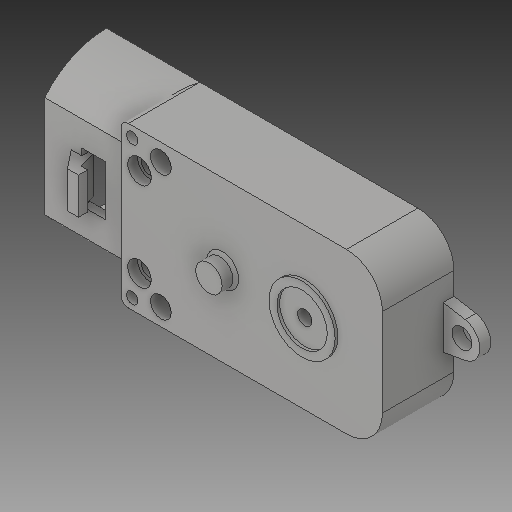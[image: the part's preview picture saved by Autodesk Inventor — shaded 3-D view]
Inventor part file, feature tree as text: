
AUTODESK INVENTOR PART (.ipt)
format: ipt  version: 2019 (Build 230136000, 136)  size: 182,784 bytes
history: mixed  units: mm
features: chamfer x1, imported_body x1
ambient origin geometry x8: Origin, YZ Plane, XZ Plane, XY Plane, X Axis, Y Axis, Z Axis, Center Point
bodies: Solid1 (imported_parasolid)
feature tree (2):
  chamfer  "Chamfer1"  [1 undecoded]
  imported_body  NMx_Import_Brep_tag  [imported B-rep: ~28 faces, bbox_mm=[44.6405, 22.225, 9.9441]]
note: 1 required parameter value undecoded (feature->parameter linkage not recoverable at this tier; creation-order binding heuristic only, values carry confidence <= 0.55)
